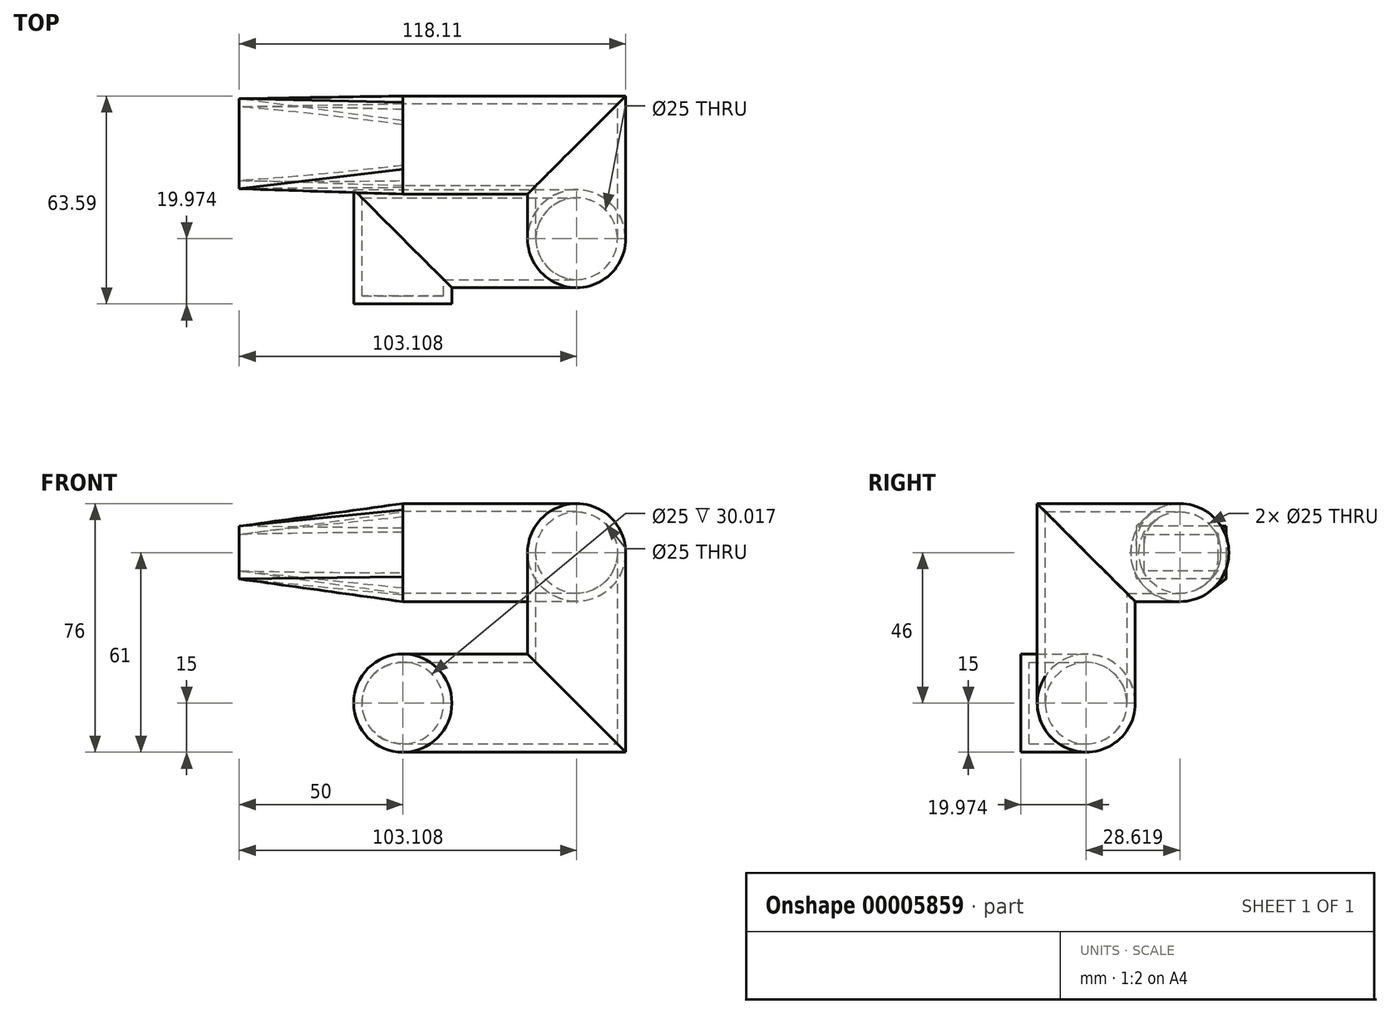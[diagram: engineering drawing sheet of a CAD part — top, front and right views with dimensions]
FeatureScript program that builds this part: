
annotation { "Feature Type Name" : "Feature", "Feature Type Description" : "" }
export const myFeature = defineFeature(function(context is Context, id is Id, definition is map)
    precondition{}
    {
        {
            var Q0;
            Q0=qCreatedBy(makeId("Front.planeOp"),FACE);
            var sketch = newSketch(context, id + "F0", { "sketchPlane" : qUnion([Q0])});
            skCircle(sketch, "E0", {"center": v(0, 0) * mm, "radius": 15 * mm});
            skSolve(sketch);
        }
        {
            var Q0;
            Q0=qCreatedBy(makeId("Top.planeOp"),FACE);
            var sketch = newSketch(context, id + "F1", { "sketchPlane" : qUnion([Q0])});
            skLineSegment(sketch, "E1", {"start": v(0, 0) * mm, "end": v(0, 19.97) * mm});
            skLineSegment(sketch, "E2", {"start": v(0, 19.97) * mm, "end": v(53.1, 19.97) * mm});
            skSolve(sketch);
        }
        {
            var Q0;
            Q0=qCreatedBy(makeId("Front.planeOp"),FACE);
            var Q1;
            Q1=sQuery(id+"F1.wireOp",VERTEX,"E2.end");
            cPlane(context, id + "F2", {"entities" : qUnion([Q0, Q1]), "cplaneType" : CPlaneType.PLANE_POINT, "offset" : 150 * mm, "width" : 150 * mm, "height" : 150 * mm});
        }
        {
            var Q0;
            Q0=qCreatedBy(id+"F2.planeOp",FACE);
            var sketch = newSketch(context, id + "F3", { "sketchPlane" : qUnion([Q0])});
            skLineSegment(sketch, "E3.0", {"start": v(0, 0) * mm, "end": v(53.1, 0) * mm});
            skLineSegment(sketch, "E4", {"start": v(53.1, 0) * mm, "end": v(53.1, 46) * mm});
            skSolve(sketch);
        }
        {
            var Q0;
            Q0=qCreatedBy(makeId("Right.planeOp"),FACE);
            var Q1;
            Q1=sQuery(id+"F3.wireOp",VERTEX,"E4.end");
            cPlane(context, id + "F4", {"entities" : qUnion([Q0, Q1]), "cplaneType" : CPlaneType.PLANE_POINT, "offset" : 150 * mm, "width" : 150 * mm, "height" : 150 * mm});
        }
        {
            var Q0;
            Q0=qCreatedBy(id+"F4.planeOp",FACE);
            var sketch = newSketch(context, id + "F5", { "sketchPlane" : qUnion([Q0])});
            skLineSegment(sketch, "E5.0", {"start": v(19.97, 0) * mm, "end": v(19.97, 46) * mm});
            skLineSegment(sketch, "E6", {"start": v(19.97, 46) * mm, "end": v(48.6, 46) * mm});
            skSolve(sketch);
        }
        {
            var Q0;
            Q0=qCreatedBy(id+"F2.planeOp",FACE);
            var Q1;
            Q1=sQuery(id+"F5.wireOp",VERTEX,"E6.end");
            cPlane(context, id + "F6", {"entities" : qUnion([Q0, Q1]), "cplaneType" : CPlaneType.PLANE_POINT, "offset" : 150 * mm, "width" : 150 * mm, "height" : 150 * mm});
        }
        {
            var Q0;
            Q0=qCreatedBy(id+"F6.planeOp",FACE);
            var sketch = newSketch(context, id + "F7", { "sketchPlane" : qUnion([Q0])});
            skLineSegment(sketch, "E7.0", {"start": v(53.1, 0) * mm, "end": v(53.1, 46) * mm});
            skLineSegment(sketch, "E8", {"start": v(53.1, 46) * mm, "end": v(0, 46) * mm});
            skSolve(sketch);
        }
        {
            var Q0;
            Q0=makeQuery(id+"F0.imprint","IMPRINT",FACE,{"disambiguationData":[TD([[makeQuery(id+"F0.imprint","IMPRINT",EDGE,{"derivedFrom":sQuery(id+"F0.wireOp",EDGE,"E0")}),1.0]])]});
            var Q1;
            Q1=sQuery(id+"F1.wireOp",EDGE,"E1");
            var Q2;
            Q2=sQuery(id+"F3.wireOp",EDGE,"E3.0");
            var Q3;
            Q3=sQuery(id+"F5.wireOp",EDGE,"E5.0");
            var Q4;
            Q4=sQuery(id+"F5.wireOp",EDGE,"E6");
            var Q5;
            Q5=sQuery(id+"F7.wireOp",EDGE,"E8");
            sweep(context, id + "F8", {"profiles" : qUnion([Q0]), "path" : qUnion([Q1, Q2, Q3, Q4, Q5])});
        }
        {
            var Q0;
            Q0=qCreatedBy(makeId("Right.planeOp"),FACE);
            cPlane(context, id + "F9", {"entities" : qUnion([Q0]), "cplaneType" : CPlaneType.OFFSET, "offset" : 50 * mm, "oppositeDirection" : true, "width" : 150 * mm, "height" : 150 * mm});
        }
        {
            var Q0;
            Q0=qCreatedBy(id+"F9.planeOp",FACE);
            var sketch = newSketch(context, id + "F10", { "sketchPlane" : qUnion([Q0])});
            skLineSegment(sketch, "E9.0.0", {"start": v(62.74, 54.07) * mm, "end": v(62.74, 37.93) * mm});
            skLineSegment(sketch, "E9.0.1", {"start": v(62.74, 54.07) * mm, "end": v(35.24, 54.07) * mm});
            skLineSegment(sketch, "E9.0.2", {"start": v(35.24, 54.07) * mm, "end": v(35.24, 37.93) * mm});
            skLineSegment(sketch, "E9.0.3", {"start": v(62.74, 37.93) * mm, "end": v(35.24, 37.93) * mm});
            skSolve(sketch);
        }
        {
            var Q0;
            Q0=makeQuery(id+"F8.opSweep","CAP_FACE",FACE,{"disambiguationData":[OSD([sQuery(id+"F0.wireOp",EDGE,"E0"),sQuery(id+"F7.wireOp",VERTEX,"E8.end")])],"isStart":false});
            var Q1;
            Q1=makeQuery(id+"F10.imprint","IMPRINT",FACE,{"disambiguationData":[TD([[makeQuery(id+"F10.imprint","IMPRINT",EDGE,{"derivedFrom":sQuery(id+"F10.wireOp",EDGE,"E9.0.0")}),-1.0]])]});
            loft(context, id + "F11", {"operationType" : NewBodyOperationType.ADD, "sheetProfilesArray" : [{ "sheetProfileEntities" : qUnion([Q0]) }, { "sheetProfileEntities" : qUnion([Q1]) }]});
        }
        {
            var Q0;
            Q0=makeQuery(id+"F11.opLoft","CAP_FACE",FACE,{"disambiguationData":[OSD([makeQuery(id+"F10.imprint","IMPRINT",FACE,{"disambiguationData":[TD([[makeQuery(id+"F10.imprint","IMPRINT",EDGE,{"derivedFrom":sQuery(id+"F10.wireOp",EDGE,"E9.0.0")}),-1.0]])]})])],"isStart":true});
            shell(context, id + "F12", {"entities" : qUnion([Q0]), "thickness" : 2.5 * mm});
        }
    });
